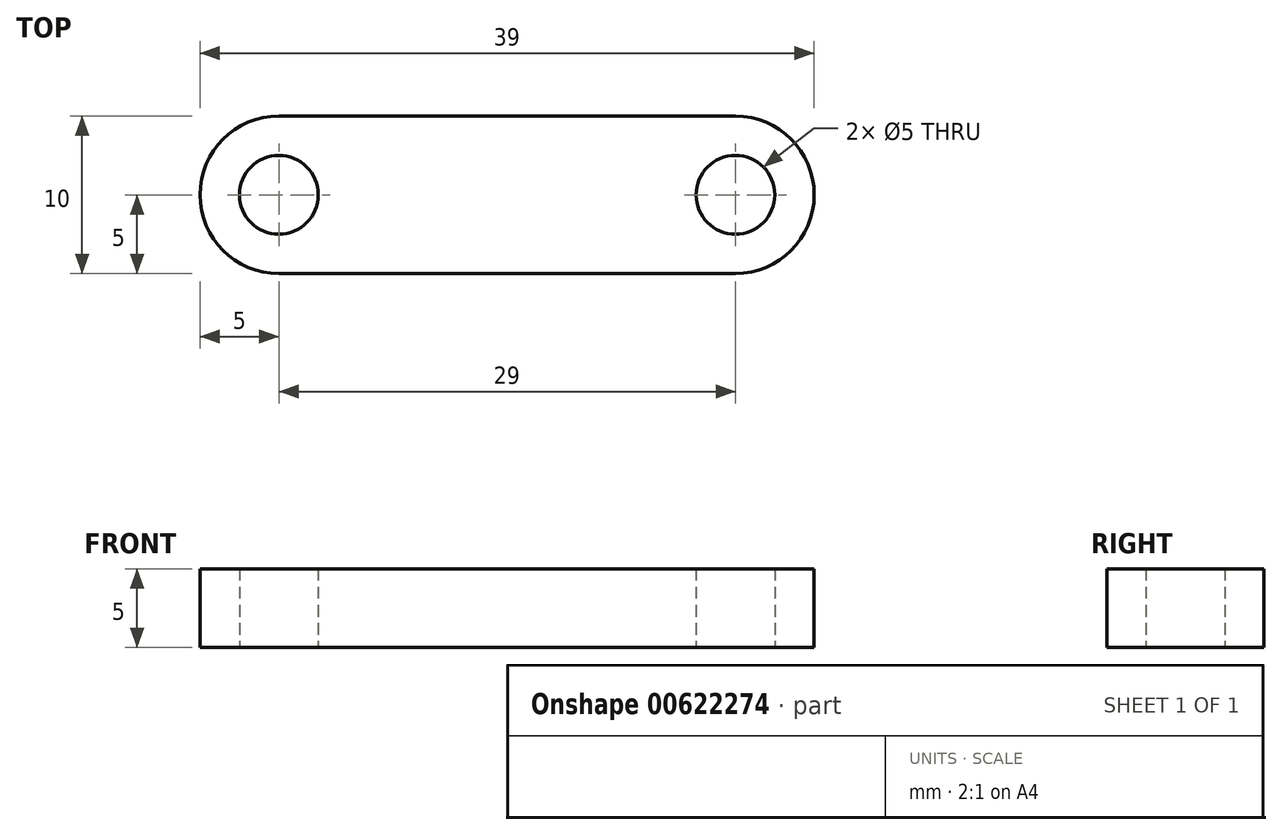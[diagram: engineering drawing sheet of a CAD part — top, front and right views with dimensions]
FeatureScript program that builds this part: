
annotation { "Feature Type Name" : "Feature", "Feature Type Description" : "" }
export const myFeature = defineFeature(function(context is Context, id is Id, definition is map)
    precondition{}
    {
        {
            var Q0;
            Q0=qCreatedBy(makeId("Top.planeOp"),FACE);
            var sketch = newSketch(context, id + "F0", { "sketchPlane" : qUnion([Q0])});
            skLineSegment(sketch, "E0", {"start": v(0, 0) * mm, "end": v(29, 0) * mm});
            skCircle(sketch, "E1", {"center": v(0, 0) * mm, "radius": 2.5 * mm});
            skCircle(sketch, "E2", {"center": v(29, 0) * mm, "radius": 2.5 * mm});
            skCircle(sketch, "E3", {"center": v(29, 0) * mm, "radius": 5 * mm});
            skCircle(sketch, "E4", {"center": v(0, 0) * mm, "radius": 5 * mm});
            skLineSegment(sketch, "E5.bottom", {"start": v(29, 5) * mm, "end": v(0, 5) * mm});
            skLineSegment(sketch, "E5.top", {"start": v(29, -5) * mm, "end": v(0, -5) * mm});
            skLineSegment(sketch, "E5.left", {"start": v(29, 5) * mm, "end": v(29, -5) * mm});
            skLineSegment(sketch, "E5.right", {"start": v(0, 5) * mm, "end": v(0, -5) * mm});
            skPoint(sketch, "E5.middle", {"position": v(14.5, 0) * mm});
            skSolve(sketch);
        }
        {
            var Q0;
            {var subQ0=sQuery(id+"F0.wireOp",EDGE,"E5.right");var subQ1=sQuery(id+"F0.wireOp",EDGE,"E1");var subQ2=makeQuery(id+"F0.imprint","INTERSECT",VERTEX,{"disambiguationData":[OD(0.0)],"derivedFrom":[subQ1,subQ0]});Q0=makeQuery(id+"F0.imprint","IMPRINT",FACE,{"disambiguationData":[TD([[makeQuery(id+"F0.imprint","IMPRINT",EDGE,{"disambiguationData":[TD([[subQ2,-1.0]])],"derivedFrom":subQ1}),-1.0]])]});}
            var Q1;
            {var subQ0=sQuery(id+"F0.wireOp",EDGE,"E1");var subQ1=sQuery(id+"F0.wireOp",EDGE,"E0");var subQ2=makeQuery(id+"F0.imprint","INTERSECT",VERTEX,{"derivedFrom":[subQ1,subQ0]});Q1=makeQuery(id+"F0.imprint","IMPRINT",FACE,{"disambiguationData":[TD([[makeQuery(id+"F0.imprint","IMPRINT",EDGE,{"disambiguationData":[TD([[subQ2,-1.0]])],"derivedFrom":subQ1}),-1.0]])]});}
            var Q2;
            {var subQ0=sQuery(id+"F0.wireOp",EDGE,"E1");var subQ1=sQuery(id+"F0.wireOp",EDGE,"E0");var subQ2=makeQuery(id+"F0.imprint","INTERSECT",VERTEX,{"derivedFrom":[subQ1,subQ0]});Q2=makeQuery(id+"F0.imprint","IMPRINT",FACE,{"disambiguationData":[TD([[makeQuery(id+"F0.imprint","IMPRINT",EDGE,{"disambiguationData":[TD([[subQ2,-1.0]])],"derivedFrom":subQ1}),1.0]])]});}
            var Q3;
            {var subQ5=sQuery(id+"F0.wireOp",EDGE,"E5.bottom");Q3=makeQuery(id+"F0.imprint","IMPRINT",FACE,{"disambiguationData":[TD([[makeQuery(id+"F0.imprint","IMPRINT",EDGE,{"derivedFrom":subQ5}),1.0]])]});}
            var Q4;
            {var subQ5=sQuery(id+"F0.wireOp",EDGE,"E5.top");Q4=makeQuery(id+"F0.imprint","IMPRINT",FACE,{"disambiguationData":[TD([[makeQuery(id+"F0.imprint","IMPRINT",EDGE,{"derivedFrom":subQ5}),-1.0]])]});}
            var Q5;
            {var subQ0=sQuery(id+"F0.wireOp",EDGE,"E3");var subQ1=sQuery(id+"F0.wireOp",EDGE,"E0");var subQ2=makeQuery(id+"F0.imprint","INTERSECT",VERTEX,{"derivedFrom":[subQ1,subQ0]});Q5=makeQuery(id+"F0.imprint","IMPRINT",FACE,{"disambiguationData":[TD([[makeQuery(id+"F0.imprint","IMPRINT",EDGE,{"disambiguationData":[TD([[subQ2,-1.0]])],"derivedFrom":subQ1}),-1.0]])]});}
            var Q6;
            {var subQ0=sQuery(id+"F0.wireOp",EDGE,"E3");var subQ1=sQuery(id+"F0.wireOp",EDGE,"E0");var subQ2=makeQuery(id+"F0.imprint","INTERSECT",VERTEX,{"derivedFrom":[subQ1,subQ0]});Q6=makeQuery(id+"F0.imprint","IMPRINT",FACE,{"disambiguationData":[TD([[makeQuery(id+"F0.imprint","IMPRINT",EDGE,{"disambiguationData":[TD([[subQ2,-1.0]])],"derivedFrom":subQ1}),1.0]])]});}
            var Q7;
            {var subQ0=sQuery(id+"F0.wireOp",EDGE,"E5.left");var subQ1=sQuery(id+"F0.wireOp",EDGE,"E2");var subQ2=makeQuery(id+"F0.imprint","INTERSECT",VERTEX,{"disambiguationData":[OD(0.0)],"derivedFrom":[subQ1,subQ0]});Q7=makeQuery(id+"F0.imprint","IMPRINT",FACE,{"disambiguationData":[TD([[makeQuery(id+"F0.imprint","IMPRINT",EDGE,{"disambiguationData":[TD([[subQ2,1.0]])],"derivedFrom":subQ1}),-1.0]])]});}
            extrude(context, id + "F1", {"entities" : qUnion([Q0, Q1, Q2, Q3, Q4, Q5, Q6, Q7]), "depth" : 5 * mm, "offsetDistance" : 25 * mm});
        }
    });
